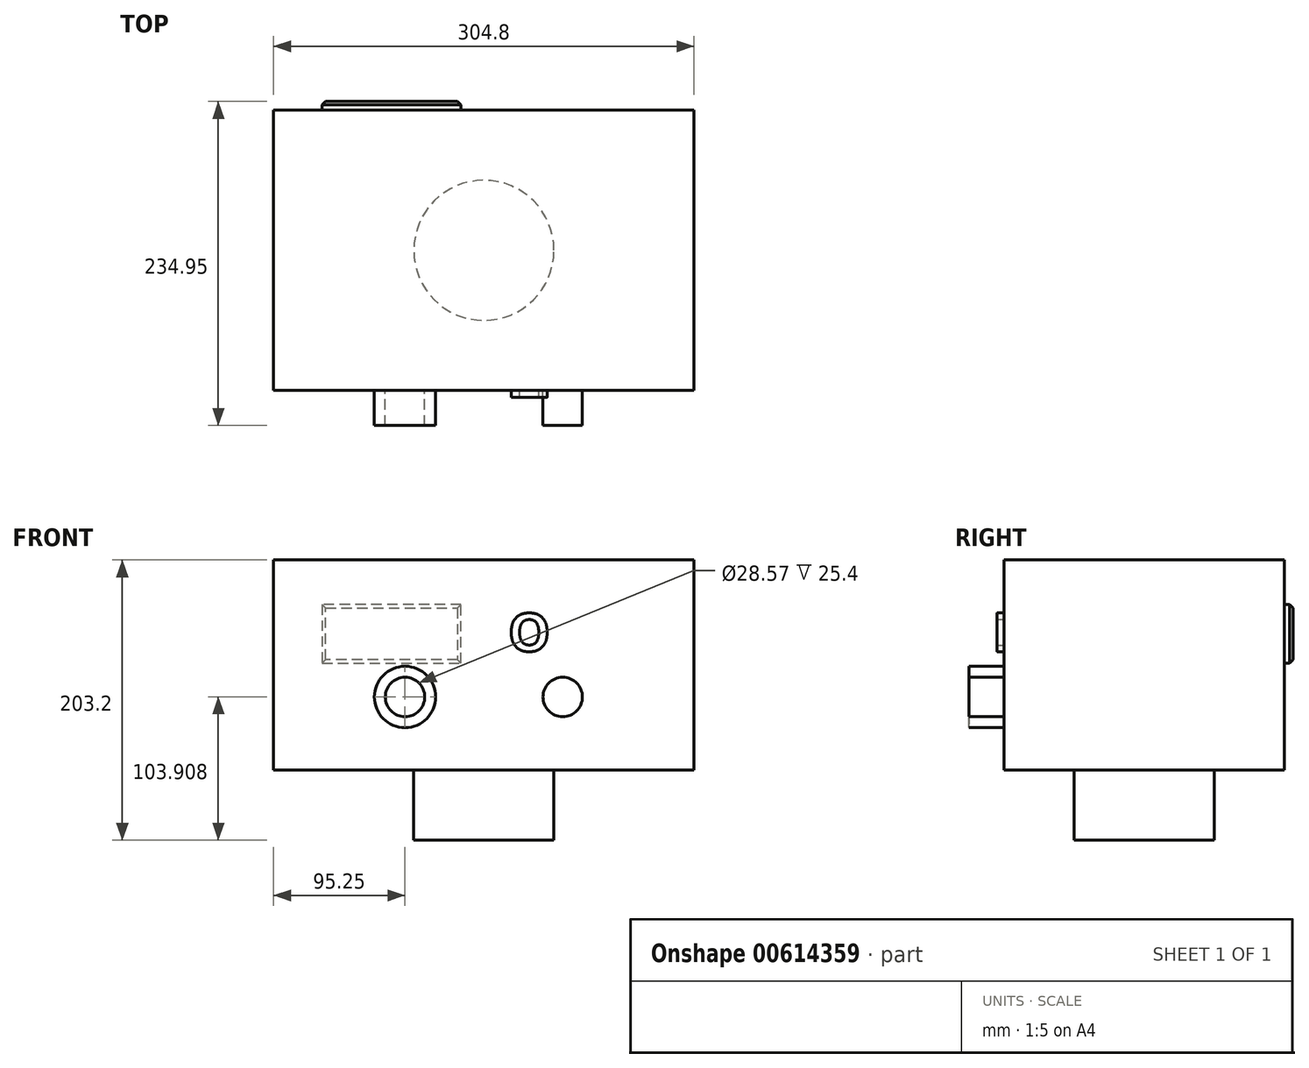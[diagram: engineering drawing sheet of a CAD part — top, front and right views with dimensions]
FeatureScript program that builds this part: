
annotation { "Feature Type Name" : "Feature", "Feature Type Description" : "" }
export const myFeature = defineFeature(function(context is Context, id is Id, definition is map)
    precondition{}
    {
        {
            var Q0;
            Q0=qCreatedBy(makeId("Top.planeOp"),FACE);
            var sketch = newSketch(context, id + "F0", { "sketchPlane" : qUnion([Q0])});
            skLineSegment(sketch, "E0", {"start": v(0, 0) * mm, "end": v(152.4, 0) * mm});
            skLineSegment(sketch, "E1", {"start": v(0, 0) * mm, "end": v(0, 101.6) * mm});
            skLineSegment(sketch, "E2", {"start": v(0, 0) * mm, "end": v(0, -101.6) * mm});
            skLineSegment(sketch, "E3", {"start": v(0, 101.6) * mm, "end": v(152.4, 101.6) * mm});
            skLineSegment(sketch, "E4", {"start": v(0, 0) * mm, "end": v(36.33, -35.5) * mm});
            skCircle(sketch, "E5", {"center": v(0, 0) * mm, "radius": 50.8 * mm});
            skLineSegment(sketch, "E6.bottom", {"start": v(152.4, 101.6) * mm, "end": v(-152.4, 101.6) * mm});
            skLineSegment(sketch, "E6.top", {"start": v(152.4, -101.6) * mm, "end": v(-152.4, -101.6) * mm});
            skLineSegment(sketch, "E6.left", {"start": v(152.4, 101.6) * mm, "end": v(152.4, -101.6) * mm});
            skLineSegment(sketch, "E6.right", {"start": v(-152.4, 101.6) * mm, "end": v(-152.4, -101.6) * mm});
            skSolve(sketch);
        }
        {
            var Q0;
            {var subQ4=sQuery(id+"F0.wireOp",EDGE,"E0");var subQ8=sQuery(id+"F0.wireOp",EDGE,"E6.left");var subQ9=makeQuery(id+"F0.imprint","INTERSECT",VERTEX,{"derivedFrom":[subQ4,subQ8]});Q0=makeQuery(id+"F0.imprint","IMPRINT",FACE,{"disambiguationData":[TD([[makeQuery(id+"F0.imprint","IMPRINT",EDGE,{"disambiguationData":[TD([[subQ9,1.0]])],"derivedFrom":subQ4}),-1.0]])]});}
            var Q1;
            {var subQ1=sQuery(id+"F0.wireOp",EDGE,"E0");var subQ7=sQuery(id+"F0.wireOp",EDGE,"E6.left");var subQ9=makeQuery(id+"F0.imprint","INTERSECT",VERTEX,{"derivedFrom":[subQ1,subQ7]});Q1=makeQuery(id+"F0.imprint","IMPRINT",FACE,{"disambiguationData":[TD([[makeQuery(id+"F0.imprint","IMPRINT",EDGE,{"disambiguationData":[TD([[subQ9,1.0]])],"derivedFrom":subQ1}),1.0]])]});}
            var Q2;
            {var subQ3=sQuery(id+"F0.wireOp",EDGE,"E6.right");Q2=makeQuery(id+"F0.imprint","IMPRINT",FACE,{"disambiguationData":[TD([[makeQuery(id+"F0.imprint","IMPRINT",EDGE,{"derivedFrom":subQ3}),1.0]])]});}
            var Q3;
            {var subQ1=sQuery(id+"F0.wireOp",EDGE,"E1");var subQ3=sQuery(id+"F0.wireOp",EDGE,"E5");var subQ4=makeQuery(id+"F0.imprint","INTERSECT",VERTEX,{"derivedFrom":[subQ1,subQ3]});Q3=makeQuery(id+"F0.imprint","IMPRINT",FACE,{"disambiguationData":[TD([[makeQuery(id+"F0.imprint","IMPRINT",EDGE,{"disambiguationData":[TD([[subQ4,-1.0]])],"derivedFrom":subQ3}),1.0]])]});}
            var Q4;
            {var subQ1=sQuery(id+"F0.wireOp",EDGE,"E0");var subQ3=sQuery(id+"F0.wireOp",EDGE,"E5");var subQ4=makeQuery(id+"F0.imprint","INTERSECT",VERTEX,{"derivedFrom":[subQ1,subQ3]});Q4=makeQuery(id+"F0.imprint","IMPRINT",FACE,{"disambiguationData":[TD([[makeQuery(id+"F0.imprint","IMPRINT",EDGE,{"disambiguationData":[TD([[subQ4,-1.0]])],"derivedFrom":subQ3}),1.0]])]});}
            var Q5;
            {var subQ0=sQuery(id+"F0.wireOp",EDGE,"E4");Q5=makeQuery(id+"F0.imprint","IMPRINT",FACE,{"disambiguationData":[TD([[makeQuery(id+"F0.imprint","IMPRINT",EDGE,{"derivedFrom":subQ0}),-1.0]])]});}
            var Q6;
            {var subQ0=sQuery(id+"F0.wireOp",EDGE,"E4");Q6=makeQuery(id+"F0.imprint","IMPRINT",FACE,{"disambiguationData":[TD([[makeQuery(id+"F0.imprint","IMPRINT",EDGE,{"derivedFrom":subQ0}),1.0]])]});}
            extrude(context, id + "F1", {"entities" : qUnion([Q0, Q1, Q2, Q3, Q4, Q5, Q6]), "depth" : 152.4 * mm, "offsetDistance" : 25.4 * mm});
        }
        {
            var Q0;
            {var subQ0=sQuery(id+"F0.wireOp",EDGE,"E4");Q0=makeQuery(id+"F0.imprint","IMPRINT",FACE,{"disambiguationData":[TD([[makeQuery(id+"F0.imprint","IMPRINT",EDGE,{"derivedFrom":subQ0}),-1.0]])]});}
            var Q1;
            {var subQ0=sQuery(id+"F0.wireOp",EDGE,"E4");Q1=makeQuery(id+"F0.imprint","IMPRINT",FACE,{"disambiguationData":[TD([[makeQuery(id+"F0.imprint","IMPRINT",EDGE,{"derivedFrom":subQ0}),1.0]])]});}
            var Q2;
            {var subQ1=sQuery(id+"F0.wireOp",EDGE,"E0");var subQ3=sQuery(id+"F0.wireOp",EDGE,"E5");var subQ4=makeQuery(id+"F0.imprint","INTERSECT",VERTEX,{"derivedFrom":[subQ1,subQ3]});Q2=makeQuery(id+"F0.imprint","IMPRINT",FACE,{"disambiguationData":[TD([[makeQuery(id+"F0.imprint","IMPRINT",EDGE,{"disambiguationData":[TD([[subQ4,-1.0]])],"derivedFrom":subQ3}),1.0]])]});}
            var Q3;
            {var subQ1=sQuery(id+"F0.wireOp",EDGE,"E1");var subQ3=sQuery(id+"F0.wireOp",EDGE,"E5");var subQ4=makeQuery(id+"F0.imprint","INTERSECT",VERTEX,{"derivedFrom":[subQ1,subQ3]});Q3=makeQuery(id+"F0.imprint","IMPRINT",FACE,{"disambiguationData":[TD([[makeQuery(id+"F0.imprint","IMPRINT",EDGE,{"disambiguationData":[TD([[subQ4,-1.0]])],"derivedFrom":subQ3}),1.0]])]});}
            extrude(context, id + "F2", {"entities" : qUnion([Q0, Q1, Q2, Q3]), "operationType" : NewBodyOperationType.ADD, "oppositeDirection" : true, "depth" : 50.8 * mm, "offsetDistance" : 25.4 * mm});
        }
        {
            var Q0;
            Q0=makeQuery(id+"F1.opExtrude","SWEPT_FACE",FACE,{"disambiguationData":[OSD([sQuery(id+"F0.wireOp",EDGE,"E6.top")])]});
            var sketch = newSketch(context, id + "F3", { "sketchPlane" : qUnion([Q0])});
            skLineSegment(sketch, "E7", {"start": v(152.4, 0) * mm, "end": v(152.4, 53.1) * mm});
            skLineSegment(sketch, "E8", {"start": v(152.4, 53.1) * mm, "end": v(-152.4, 53.1) * mm});
            skLineSegment(sketch, "E9", {"start": v(-152.4, 53.1) * mm, "end": v(-57.15, 53.1) * mm});
            skLineSegment(sketch, "E10", {"start": v(152.4, 53.1) * mm, "end": v(57.15, 53.1) * mm});
            skCircle(sketch, "E11", {"center": v(-57.15, 53.1) * mm, "radius": 22.23 * mm});
            skCircle(sketch, "E12", {"center": v(57.15, 53.1) * mm, "radius": 22.23 * mm});
            skCircle(sketch, "E13", {"center": v(-57.15, 53.1) * mm, "radius": 14.29 * mm});
            skCircle(sketch, "E14", {"center": v(57.15, 53.1) * mm, "radius": 14.29 * mm});
            skSolve(sketch);
        }
        {
            var Q0;
            {var subQ0=sQuery(id+"F3.wireOp",EDGE,"E14");var subQ1=sQuery(id+"F3.wireOp",EDGE,"E8");var subQ2=makeQuery(id+"F3.imprint","INTERSECT",VERTEX,{"derivedFrom":[subQ1,subQ0]});Q0=makeQuery(id+"F3.imprint","IMPRINT",FACE,{"disambiguationData":[TD([[makeQuery(id+"F3.imprint","IMPRINT",EDGE,{"disambiguationData":[TD([[subQ2,-1.0]])],"derivedFrom":subQ1}),-1.0]])]});}
            var Q1;
            {var subQ0=sQuery(id+"F3.wireOp",EDGE,"E14");var subQ1=sQuery(id+"F3.wireOp",EDGE,"E8");var subQ2=makeQuery(id+"F3.imprint","INTERSECT",VERTEX,{"derivedFrom":[subQ1,subQ0]});Q1=makeQuery(id+"F3.imprint","IMPRINT",FACE,{"disambiguationData":[TD([[makeQuery(id+"F3.imprint","IMPRINT",EDGE,{"disambiguationData":[TD([[subQ2,-1.0]])],"derivedFrom":subQ1}),1.0]])]});}
            var Q2;
            {var subQ0=sQuery(id+"F3.wireOp",EDGE,"E11");var subQ1=sQuery(id+"F3.wireOp",EDGE,"E8");var subQ2=makeQuery(id+"F3.imprint","INTERSECT",VERTEX,{"derivedFrom":[subQ1,subQ0]});Q2=makeQuery(id+"F3.imprint","IMPRINT",FACE,{"disambiguationData":[TD([[makeQuery(id+"F3.imprint","IMPRINT",EDGE,{"disambiguationData":[TD([[subQ2,-1.0]])],"derivedFrom":subQ1}),-1.0]])]});}
            var Q3;
            {var subQ0=sQuery(id+"F3.wireOp",EDGE,"E11");var subQ1=sQuery(id+"F3.wireOp",EDGE,"E8");var subQ2=makeQuery(id+"F3.imprint","INTERSECT",VERTEX,{"derivedFrom":[subQ1,subQ0]});Q3=makeQuery(id+"F3.imprint","IMPRINT",FACE,{"disambiguationData":[TD([[makeQuery(id+"F3.imprint","IMPRINT",EDGE,{"disambiguationData":[TD([[subQ2,-1.0]])],"derivedFrom":subQ1}),1.0]])]});}
            var Q4;
            Q4=sQuery(id+"F3.wireOp",EDGE,"E12");
            var Q5;
            Q5=sQuery(id+"F3.wireOp",EDGE,"E14");
            var Q6;
            Q6=sQuery(id+"F3.wireOp",EDGE,"E11");
            var Q7;
            Q7=sQuery(id+"F3.wireOp",EDGE,"E13");
            extrude(context, id + "F4", {"entities" : qUnion([Q0, Q1, Q2, Q3]), "operationType" : NewBodyOperationType.ADD, "surfaceEntities" : qUnion([Q4, Q5, Q6, Q7]), "depth" : 25.4 * mm, "offsetDistance" : 25.4 * mm});
        }
        {
            var Q0;
            Q0=makeQuery(id+"F1.opExtrude","SWEPT_FACE",FACE,{"disambiguationData":[OSD([sQuery(id+"F0.wireOp",EDGE,"E6.bottom")])]});
            var sketch = newSketch(context, id + "F5", { "sketchPlane" : qUnion([Q0])});
            skLineSegment(sketch, "E15.bottom", {"start": v(16.6, 77.64) * mm, "end": v(117.3, 77.64) * mm});
            skLineSegment(sketch, "E15.top", {"start": v(16.6, 120) * mm, "end": v(117.3, 120) * mm});
            skLineSegment(sketch, "E15.left", {"start": v(16.6, 77.64) * mm, "end": v(16.6, 120) * mm});
            skLineSegment(sketch, "E15.right", {"start": v(117.3, 77.64) * mm, "end": v(117.3, 120) * mm});
            skSolve(sketch);
        }
        {
            var Q0;
            Q0=makeQuery(id+"F5.imprint","IMPRINT",FACE,{"disambiguationData":[TD([[makeQuery(id+"F5.imprint","IMPRINT",EDGE,{"derivedFrom":sQuery(id+"F5.wireOp",EDGE,"E15.bottom")}),1.0]])]});
            extrude(context, id + "F6", {"entities" : qUnion([Q0]), "depth" : 6.35 * mm, "offsetDistance" : 25.4 * mm});
        }
        {
            var Q0;
            Q0=makeQuery(id+"F6.opExtrude","CAP_EDGE",EDGE,{"disambiguationData":[OSD([sQuery(id+"F5.wireOp",EDGE,"E15.top")])],"isStart":false});
            var Q1;
            Q1=makeQuery(id+"F6.opExtrude","CAP_EDGE",EDGE,{"disambiguationData":[OSD([sQuery(id+"F5.wireOp",EDGE,"E15.right")])],"isStart":false});
            var Q2;
            Q2=makeQuery(id+"F6.opExtrude","CAP_EDGE",EDGE,{"disambiguationData":[OSD([sQuery(id+"F5.wireOp",EDGE,"E15.left")])],"isStart":false});
            var Q3;
            Q3=makeQuery(id+"F6.opExtrude","CAP_EDGE",EDGE,{"disambiguationData":[OSD([sQuery(id+"F5.wireOp",EDGE,"E15.bottom")])],"isStart":false});
            chamfer(context, id + "F7", {"entities" : qUnion([Q0, Q1, Q2, Q3]), "width" : 2.54 * mm, "tangentPropagation" : true});
        }
        {
            var Q0;
            {var subQ1=sQuery(id+"F0.wireOp",EDGE,"E6.left");var subQ2=sQuery(id+"F0.wireOp",EDGE,"E6.top");Q0=makeQuery(id+"F4.boolean.opBoolean","SPLIT",FACE,{"disambiguationData":[TD([makeQuery(id+"F1.opExtrude","SWEPT_FACE",FACE,{"disambiguationData":[OSD([subQ1])]})])],"derivedFrom":makeQuery(id+"F1.opExtrude","SWEPT_FACE",FACE,{"disambiguationData":[OSD([subQ2])]})});}
            var sketch = newSketch(context, id + "F8", { "sketchPlane" : qUnion([Q0])});
            skText(sketch, "E16", { "text": "OUT", "fontName": "OpenSans-Bold.ttf"});
            const initialGuessF8  = {"E16": [0.0176, 0.08625, 1, 0, 0.0276]};
            skSetInitialGuess(sketch, initialGuessF8);
            skSolve(sketch);
        }
        {
            var Q0;
            Q0=makeQuery(id+"F8.imprint","IMPRINT",FACE,{"disambiguationData":[TD([[makeQuery(id+"F8.imprint","IMPRINT",EDGE,{"derivedFrom":sQuery(id+"F8.wireOp",EDGE,"E16.sketch_text.stroke-0")}),1.0]])]});
            var sketch = newSketch(context, id + "F9", { "sketchPlane" : qUnion([Q0])});
            skSolve(sketch);
        }
        {
            var Q0;
            Q0 = qSketchRegion(id + "F9", true);
            var Q1;
            Q1=makeQuery(id+"F9.imprint","IMPRINT",FACE,{"disambiguationData":[TD([[makeQuery(id+"F9.imprint","IMPRINT",EDGE,{"derivedFrom":makeQuery(id+"F8.imprint","IMPRINT",EDGE,{"derivedFrom":sQuery(id+"F8.wireOp",EDGE,"E16.sketch_text.stroke-29")})}),-1.0]])]});
            var Q2;
            Q2=makeQuery(id+"F9.imprint","IMPRINT",FACE,{"disambiguationData":[TD([[makeQuery(id+"F9.imprint","IMPRINT",EDGE,{"derivedFrom":makeQuery(id+"F8.imprint","IMPRINT",EDGE,{"derivedFrom":sQuery(id+"F8.wireOp",EDGE,"E16.sketch_text.stroke-14")})}),-1.0]])]});
            var Q3;
            Q3=makeQuery(id+"F8.imprint","IMPRINT",FACE,{"disambiguationData":[TD([[makeQuery(id+"F8.imprint","IMPRINT",EDGE,{"derivedFrom":sQuery(id+"F8.wireOp",EDGE,"E16.sketch_text.stroke-0")}),-1.0]])]});
            extrude(context, id + "F10", {"entities" : qUnion([Q0, Q1, Q2, Q3]), "operationType" : NewBodyOperationType.ADD, "depth" : 5.08 * mm, "offsetDistance" : 25.4 * mm});
        }
    });
